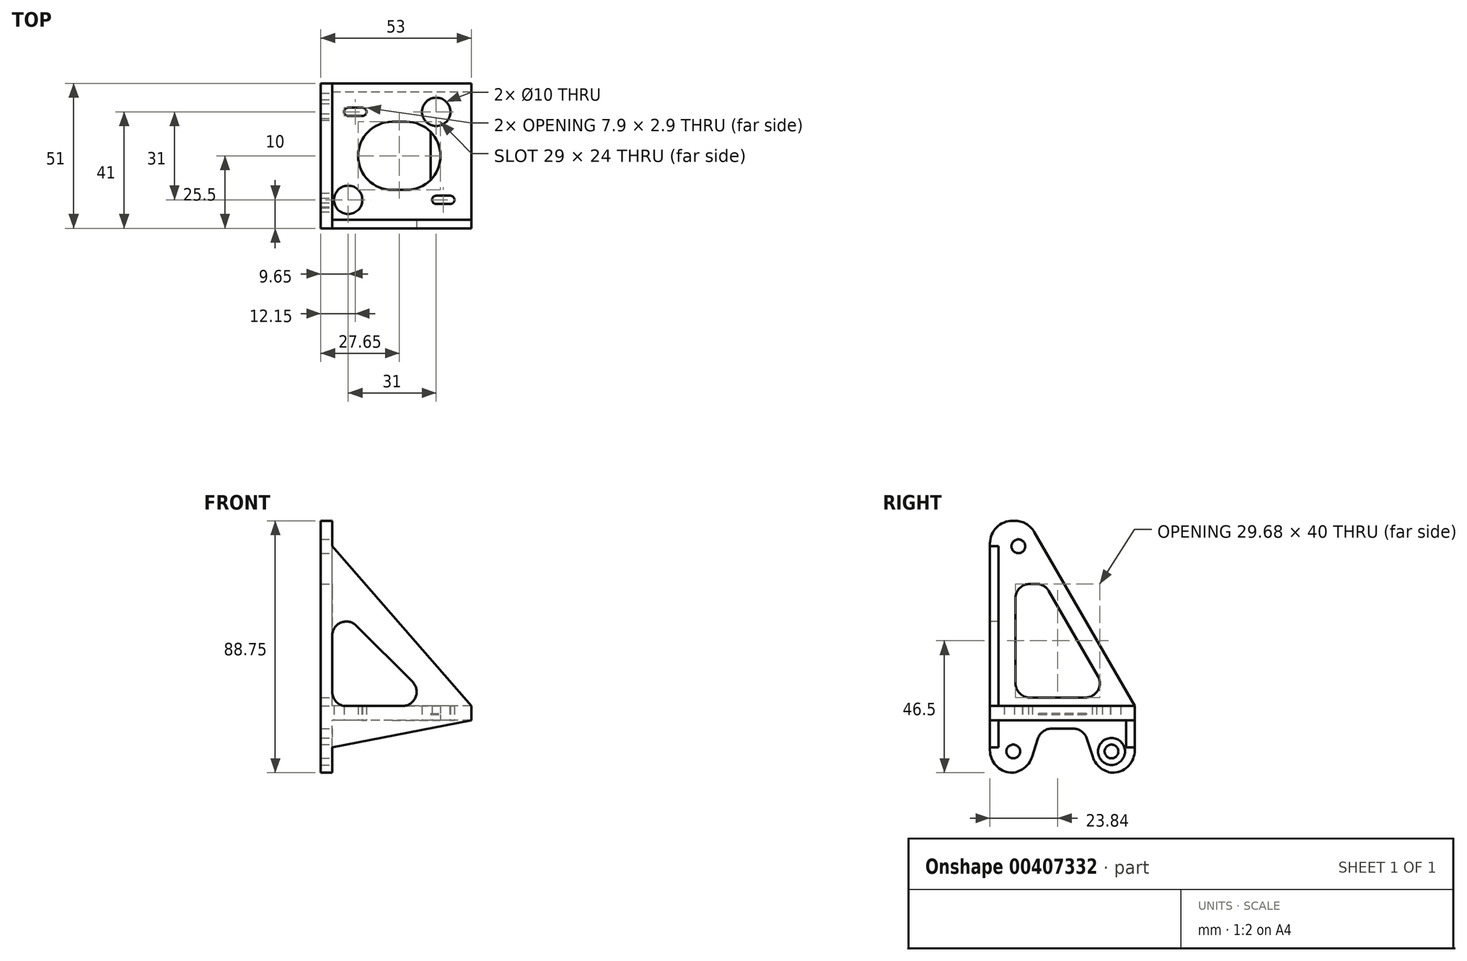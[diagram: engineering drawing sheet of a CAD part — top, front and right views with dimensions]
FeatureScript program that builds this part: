
annotation { "Feature Type Name" : "Feature", "Feature Type Description" : "" }
export const myFeature = defineFeature(function(context is Context, id is Id, definition is map)
    precondition{}
    {
        {
            var Q0;
            Q0=qCreatedBy(makeId("Right.planeOp"),FACE);
            var sketch = newSketch(context, id + "F0", { "sketchPlane" : qUnion([Q0])});
            skLineSegment(sketch, "E0", {"start": v(80, -40) * mm, "end": v(-40, -40) * mm, "construction": true});
            skLineSegment(sketch, "E1", {"start": v(-40, -40) * mm, "end": v(-40, 0) * mm, "construction": true});
            skLineSegment(sketch, "E2", {"start": v(-40, 0) * mm, "end": v(80, 0) * mm, "construction": true});
            skLineSegment(sketch, "E3", {"start": v(80, 0) * mm, "end": v(80, -40) * mm, "construction": true});
            skLineSegment(sketch, "E4", {"start": v(-40, 0) * mm, "end": v(0, 0) * mm, "construction": true});
            skLineSegment(sketch, "E5", {"start": v(0, 0) * mm, "end": v(0, 120) * mm, "construction": true});
            skLineSegment(sketch, "E6", {"start": v(0, 120) * mm, "end": v(-40, 120) * mm, "construction": true});
            skLineSegment(sketch, "E7", {"start": v(-40, 120) * mm, "end": v(-40, 0) * mm, "construction": true});
            skLineSegment(sketch, "E8", {"start": v(-20, -40) * mm, "end": v(-20, 0) * mm, "construction": true});
            skLineSegment(sketch, "E9", {"start": v(-20, -30) * mm, "end": v(-40, -30) * mm, "construction": true});
            skLineSegment(sketch, "E10", {"start": v(-14.5, -34.55) * mm, "end": v(-21.03, -34.55) * mm, "construction": true});
            skLineSegment(sketch, "E11", {"start": v(-21.03, -34.55) * mm, "end": v(-21.03, -33.52) * mm, "construction": true});
            skLineSegment(sketch, "E12", {"start": v(-14.5, -34.55) * mm, "end": v(-14.5, -20.46) * mm, "construction": true});
            skLineSegment(sketch, "E13", {"start": v(-21.03, -33.52) * mm, "end": v(-19.25, -33.52) * mm, "construction": true});
            skLineSegment(sketch, "E14", {"start": v(-19.25, -33.52) * mm, "end": v(-19.25, -26.47) * mm, "construction": true});
            skLineSegment(sketch, "E15", {"start": v(-19.25, -26.48) * mm, "end": v(-21.03, -26.48) * mm, "construction": true});
            skLineSegment(sketch, "E16", {"start": v(-21.03, -26.47) * mm, "end": v(-21.03, -20.46) * mm, "construction": true});
            skLineSegment(sketch, "E17", {"start": v(-21.03, -20.46) * mm, "end": v(-14.5, -20.46) * mm, "construction": true});
            skLineSegment(sketch, "E18", {"start": v(-20, -33.1) * mm, "end": v(-18.6, -33.1) * mm, "construction": true});
            skLineSegment(sketch, "E19", {"start": v(-18.6, -33.1) * mm, "end": v(-18.6, -26.9) * mm, "construction": true});
            skLineSegment(sketch, "E20", {"start": v(-18.6, -26.9) * mm, "end": v(-20, -26.9) * mm, "construction": true});
            skLineSegment(sketch, "E21", {"start": v(-20, -26.9) * mm, "end": v(-20, -33.1) * mm, "construction": true});
            skLineSegment(sketch, "E22", {"start": v(-14.5, -30) * mm, "end": v(-20, -30) * mm, "construction": true});
            skPoint(sketch, "E22.endSnap0", {"position": v(-20, -30) * mm});
            skLineSegment(sketch, "E23.MirrorCS", {"start": v(-14.5, -34.55) * mm, "end": v(-7.98, -34.55) * mm, "construction": true});
            skLineSegment(sketch, "E24.MirrorCS", {"start": v(-7.98, -34.55) * mm, "end": v(-7.98, -33.52) * mm, "construction": true});
            skLineSegment(sketch, "E25.MirrorCS", {"start": v(-7.98, -33.52) * mm, "end": v(-9.75, -33.52) * mm, "construction": true});
            skLineSegment(sketch, "E26.MirrorCS", {"start": v(-9.75, -33.52) * mm, "end": v(-9.75, -26.47) * mm, "construction": true});
            skLineSegment(sketch, "E27.MirrorCS", {"start": v(-10.4, -33.1) * mm, "end": v(-10.4, -26.9) * mm, "construction": true});
            skLineSegment(sketch, "E28.MirrorCS", {"start": v(-9, -26.9) * mm, "end": v(-9, -33.1) * mm, "construction": true});
            skLineSegment(sketch, "E29.MirrorCS", {"start": v(-9, -33.1) * mm, "end": v(-10.4, -33.1) * mm, "construction": true});
            skLineSegment(sketch, "E30.MirrorCS", {"start": v(-10.4, -26.9) * mm, "end": v(-9, -26.9) * mm, "construction": true});
            skLineSegment(sketch, "E31.MirrorCS", {"start": v(-9.75, -26.48) * mm, "end": v(-7.98, -26.48) * mm, "construction": true});
            skLineSegment(sketch, "E32.MirrorCS", {"start": v(-7.98, -26.47) * mm, "end": v(-7.98, -20.46) * mm, "construction": true});
            skLineSegment(sketch, "E33.MirrorCS", {"start": v(-7.98, -20.46) * mm, "end": v(-14.5, -20.46) * mm, "construction": true});
            skLineSegment(sketch, "E34", {"start": v(-37.22, -33.1) * mm, "end": v(14.04, -33.1) * mm, "construction": true});
            skLineSegment(sketch, "E35.MirrorCS", {"start": v(-37.22, -26.9) * mm, "end": v(14.04, -26.9) * mm, "construction": true});
            skLineSegment(sketch, "E36", {"start": v(-10, 0) * mm, "end": v(-10, 120) * mm, "construction": true});
            skLineSegment(sketch, "E37", {"start": v(-6.9, 0) * mm, "end": v(-6.9, 120) * mm, "construction": true});
            skLineSegment(sketch, "E38", {"start": v(-13.1, 120) * mm, "end": v(-13.1, 0) * mm, "construction": true});
            skLineSegment(sketch, "E39.MirrorCS", {"start": v(-26.9, 120) * mm, "end": v(-26.9, 0) * mm, "construction": true});
            skLineSegment(sketch, "E40.MirrorCS", {"start": v(-33.1, 0) * mm, "end": v(-33.1, 120) * mm, "construction": true});
            skLineSegment(sketch, "E41", {"start": v(6.62, -14) * mm, "end": v(-35.63, -14) * mm, "construction": true});
            skLineSegment(sketch, "E42", {"start": v(-35.63, -14) * mm, "end": v(-35.63, 33.25) * mm, "construction": true});
            skLineSegment(sketch, "E43", {"start": v(-35.63, 33.25) * mm, "end": v(6.62, 33.25) * mm, "construction": true});
            skLineSegment(sketch, "E44", {"start": v(6.62, 33.25) * mm, "end": v(6.63, -14) * mm, "construction": true});
            skLineSegment(sketch, "E45", {"start": v(-14.5, -14) * mm, "end": v(-14.5, 33.25) * mm, "construction": true});
            skLineSegment(sketch, "E46", {"start": v(-1, -14) * mm, "end": v(-1, -10) * mm, "construction": true});
            skLineSegment(sketch, "E47", {"start": v(3, -10) * mm, "end": v(-1, -10) * mm, "construction": true});
            skLineSegment(sketch, "E48", {"start": v(3, -10) * mm, "end": v(3, -14) * mm, "construction": true});
            skLineSegment(sketch, "E49", {"start": v(1, -10) * mm, "end": v(1, -14) * mm, "construction": true});
            skLineSegment(sketch, "E50.MirrorCS", {"start": v(-32, -10) * mm, "end": v(-32, -14) * mm, "construction": true});
            skLineSegment(sketch, "E51.MirrorCS", {"start": v(-32, -10) * mm, "end": v(-28, -10) * mm, "construction": true});
            skLineSegment(sketch, "E52.MirrorCS", {"start": v(-30, -10) * mm, "end": v(-30, -14) * mm, "construction": true});
            skLineSegment(sketch, "E53.MirrorCS", {"start": v(-28, -14) * mm, "end": v(-28, -10) * mm, "construction": true});
            skLineSegment(sketch, "E54", {"start": v(-3.5, -14) * mm, "end": v(-3.5, -16) * mm, "construction": true});
            skLineSegment(sketch, "E55", {"start": v(-3.5, -16) * mm, "end": v(-25.5, -16) * mm, "construction": true});
            skLineSegment(sketch, "E56", {"start": v(-25.5, -16) * mm, "end": v(-25.5, -14) * mm, "construction": true});
            skLineSegment(sketch, "E57", {"start": v(-12.25, -16) * mm, "end": v(-12.25, -38) * mm, "construction": true});
            skLineSegment(sketch, "E58", {"start": v(-12.25, -38) * mm, "end": v(-16.75, -38) * mm, "construction": true});
            skLineSegment(sketch, "E59", {"start": v(-16.75, -38) * mm, "end": v(-16.75, -16) * mm, "construction": true});
            skLineSegment(sketch, "E60", {"start": v(-31.3, 51.25) * mm, "end": v(-40, 51.25) * mm});
            skLineSegment(sketch, "E61", {"start": v(-40, 51.25) * mm, "end": v(-40, -37.5) * mm});
            skLineSegment(sketch, "E62", {"start": v(-40, -37.5) * mm, "end": v(-32.83, -37.5) * mm});
            skLineSegment(sketch, "E63", {"start": v(-25.21, -31.96) * mm, "end": v(-23.12, -25.46) * mm});
            skLineSegment(sketch, "E64", {"start": v(3.83, -37.5) * mm, "end": v(11, -37.5) * mm});
            skLineSegment(sketch, "E65", {"start": v(11, -37.5) * mm, "end": v(11, -14) * mm});
            skCircle(sketch, "E66", {"center": v(-31.8, -30) * mm, "radius": 2.43 * mm});
            skCircle(sketch, "E67.MirrorC", {"center": v(2.8, -30) * mm, "radius": 2.43 * mm});
            skLineSegment(sketch, "E68", {"start": v(-37, -37.5) * mm, "end": v(-37, 51.25) * mm});
            skLineSegment(sketch, "E69", {"start": v(-37, -14) * mm, "end": v(11, -14) * mm});
            skLineSegment(sketch, "E70.MirrorCS", {"start": v(-3.79, -31.96) * mm, "end": v(-5.88, -25.46) * mm});
            skLineSegment(sketch, "E71", {"start": v(-10.64, -22) * mm, "end": v(-18.36, -22) * mm});
            skCircle(sketch, "E72", {"center": v(-31.8, -30) * mm, "radius": 4.75 * mm});
            skCircle(sketch, "E73.MirrorC", {"center": v(2.8, -30) * mm, "radius": 4.75 * mm});
            skLineSegment(sketch, "E74", {"start": v(-37, -19) * mm, "end": v(11, -19) * mm});
            skLineSegment(sketch, "E75.MirrorCS", {"start": v(8, -37.5) * mm, "end": v(8, -14) * mm});
            skCircle(sketch, "E76", {"center": v(-30, 42.25) * mm, "radius": 2.43 * mm});
            skCircle(sketch, "E77", {"center": v(-30, 42.25) * mm, "radius": 4.75 * mm, "construction": true});
            skLineSegment(sketch, "E78", {"start": v(-30, 0) * mm, "end": v(-30, 120) * mm, "construction": true});
            skLineSegment(sketch, "E79", {"start": v(11, -14) * mm, "end": v(-24.36, 47.25) * mm});
            skLineSegment(sketch, "E80", {"start": v(-6.32, -11) * mm, "end": v(-26, -11) * mm});
            skLineSegment(sketch, "E81", {"start": v(-31, -6) * mm, "end": v(-31, 24) * mm});
            skLineSegment(sketch, "E82", {"start": v(-19.31, 26.5) * mm, "end": v(-2, -3.5) * mm});
            skArc(sketch, "E83.filletArc", {"start": v(-6.32, -11) * mm, "mid": v(-2, -8.5) * mm, "end": v(-2, -3.5) * mm});
            skArc(sketch, "E84.filletArc", {"start": v(-31, -6) * mm, "mid": v(-29.54, -9.54) * mm, "end": v(-26, -11) * mm});
            skLineSegment(sketch, "E85", {"start": v(-23.64, 29) * mm, "end": v(-26, 29) * mm});
            skArc(sketch, "E86.filletArc", {"start": v(-26, 29) * mm, "mid": v(-29.54, 27.54) * mm, "end": v(-31, 24) * mm});
            skPoint(sketch, "E87.visualSharp", {"position": v(-20.75, 29) * mm});
            skArc(sketch, "E87.filletArc", {"start": v(-19.31, 26.5) * mm, "mid": v(-21.14, 28.33) * mm, "end": v(-23.64, 29) * mm});
            skPoint(sketch, "E88.visualSharp", {"position": v(-7, -22) * mm});
            skArc(sketch, "E88.filletArc", {"start": v(-5.88, -25.46) * mm, "mid": v(-7.7, -22.96) * mm, "end": v(-10.64, -22) * mm});
            skPoint(sketch, "E89.visualSharp", {"position": v(-22, -22) * mm});
            skArc(sketch, "E89.filletArc", {"start": v(-18.36, -22) * mm, "mid": v(-21.3, -22.96) * mm, "end": v(-23.12, -25.46) * mm});
            skPoint(sketch, "E90.visualSharp", {"position": v(-2, -37.5) * mm});
            skArc(sketch, "E90.filletArc", {"start": v(-3.79, -31.96) * mm, "mid": v(-0.88, -35.97) * mm, "end": v(3.83, -37.5) * mm});
            skPoint(sketch, "E91.visualSharp", {"position": v(-27, -37.5) * mm});
            skArc(sketch, "E91.filletArc", {"start": v(-32.83, -37.5) * mm, "mid": v(-28.12, -35.97) * mm, "end": v(-25.21, -31.96) * mm});
            skPoint(sketch, "E92.visualSharp", {"position": v(-26.67, 51.25) * mm});
            skArc(sketch, "E92.filletArc", {"start": v(-24.36, 47.25) * mm, "mid": v(-27.3, 50.18) * mm, "end": v(-31.3, 51.25) * mm});
            skSolve(sketch);
        }
        {
            var Q0;
            Q0=makeQuery(id+"F0.imprint","IMPRINT",FACE,{"disambiguationData":[TD([[makeQuery(id+"F0.imprint","IMPRINT",EDGE,{"derivedFrom":sQuery(id+"F0.wireOp",EDGE,"E76")}),-1.0]])]});
            var Q1;
            {var subQ6=sQuery(id+"F0.wireOp",EDGE,"E63");Q1=makeQuery(id+"F0.imprint","IMPRINT",FACE,{"disambiguationData":[TD([[makeQuery(id+"F0.imprint","IMPRINT",EDGE,{"derivedFrom":subQ6}),1.0]])]});}
            var Q2;
            {var subQ0=sQuery(id+"F0.wireOp",EDGE,"E65");var subQ1=sQuery(id+"F0.wireOp",EDGE,"E64");var subQ2=makeQuery(id+"F0.imprint","INTERSECT",VERTEX,{"derivedFrom":[subQ1,subQ0]});Q2=makeQuery(id+"F0.imprint","IMPRINT",FACE,{"disambiguationData":[TD([[makeQuery(id+"F0.imprint","IMPRINT",EDGE,{"disambiguationData":[TD([[subQ2,1.0]])],"derivedFrom":subQ1}),1.0]])]});}
            var Q3;
            {var subQ1=sQuery(id+"F0.wireOp",EDGE,"E65");var subQ3=sQuery(id+"F0.wireOp",EDGE,"E74");var subQ4=makeQuery(id+"F0.imprint","INTERSECT",VERTEX,{"derivedFrom":[subQ1,subQ3]});Q3=makeQuery(id+"F0.imprint","IMPRINT",FACE,{"disambiguationData":[TD([[makeQuery(id+"F0.imprint","IMPRINT",EDGE,{"disambiguationData":[TD([[subQ4,1.0]])],"derivedFrom":subQ3}),1.0]])]});}
            var Q4;
            {var subQ0=sQuery(id+"F0.wireOp",EDGE,"E69");var subQ1=sQuery(id+"F0.wireOp",EDGE,"E68");var subQ2=makeQuery(id+"F0.imprint","INTERSECT",VERTEX,{"derivedFrom":[subQ1,subQ0]});Q4=makeQuery(id+"F0.imprint","IMPRINT",FACE,{"disambiguationData":[TD([[makeQuery(id+"F0.imprint","IMPRINT",EDGE,{"disambiguationData":[TD([[subQ2,1.0]])],"derivedFrom":subQ1}),-1.0]])]});}
            var Q5;
            {var subQ1=sQuery(id+"F0.wireOp",EDGE,"E61");Q5=makeQuery(id+"F0.imprint","IMPRINT",FACE,{"disambiguationData":[TD([[makeQuery(id+"F0.imprint","IMPRINT",EDGE,{"derivedFrom":subQ1}),1.0]])]});}
            var Q6;
            Q6=makeQuery(id+"F0.imprint","IMPRINT",FACE,{"disambiguationData":[TD([[makeQuery(id+"F0.imprint","IMPRINT",EDGE,{"derivedFrom":sQuery(id+"F0.wireOp",EDGE,"E67.MirrorC")}),1.0]])]});
            var Q7;
            Q7=makeQuery(id+"F0.imprint","IMPRINT",FACE,{"disambiguationData":[TD([[makeQuery(id+"F0.imprint","IMPRINT",EDGE,{"derivedFrom":sQuery(id+"F0.wireOp",EDGE,"E66")}),-1.0]])]});
            extrude(context, id + "F1", {"entities" : qUnion([Q0, Q1, Q2, Q3, Q4, Q5, Q6, Q7]), "oppositeDirection" : true, "depth" : 4 * mm});
        }
        {
            var Q0;
            {var subQ1=sQuery(id+"F0.wireOp",EDGE,"E61");Q0=makeQuery(id+"F0.imprint","IMPRINT",FACE,{"disambiguationData":[TD([[makeQuery(id+"F0.imprint","IMPRINT",EDGE,{"derivedFrom":subQ1}),1.0]])]});}
            var Q1;
            {var subQ0=sQuery(id+"F0.wireOp",EDGE,"E65");var subQ1=sQuery(id+"F0.wireOp",EDGE,"E64");var subQ2=makeQuery(id+"F0.imprint","INTERSECT",VERTEX,{"derivedFrom":[subQ1,subQ0]});Q1=makeQuery(id+"F0.imprint","IMPRINT",FACE,{"disambiguationData":[TD([[makeQuery(id+"F0.imprint","IMPRINT",EDGE,{"disambiguationData":[TD([[subQ2,1.0]])],"derivedFrom":subQ1}),1.0]])]});}
            var Q2;
            {var subQ1=sQuery(id+"F0.wireOp",EDGE,"E65");var subQ3=sQuery(id+"F0.wireOp",EDGE,"E74");var subQ4=makeQuery(id+"F0.imprint","INTERSECT",VERTEX,{"derivedFrom":[subQ1,subQ3]});Q2=makeQuery(id+"F0.imprint","IMPRINT",FACE,{"disambiguationData":[TD([[makeQuery(id+"F0.imprint","IMPRINT",EDGE,{"disambiguationData":[TD([[subQ4,1.0]])],"derivedFrom":subQ3}),1.0]])]});}
            var Q3;
            {var subQ0=sQuery(id+"F0.wireOp",EDGE,"E69");var subQ1=sQuery(id+"F0.wireOp",EDGE,"E68");var subQ2=makeQuery(id+"F0.imprint","INTERSECT",VERTEX,{"derivedFrom":[subQ1,subQ0]});Q3=makeQuery(id+"F0.imprint","IMPRINT",FACE,{"disambiguationData":[TD([[makeQuery(id+"F0.imprint","IMPRINT",EDGE,{"disambiguationData":[TD([[subQ2,1.0]])],"derivedFrom":subQ1}),-1.0]])]});}
            extrude(context, id + "F2", {"entities" : qUnion([Q0, Q1, Q2, Q3]), "operationType" : NewBodyOperationType.ADD, "offsetDistance" : 25 * mm, "depth" : 49 * mm});
        }
        {
            var Q0;
            {var subQ0=sQuery(id+"F0.wireOp",EDGE,"E61");Q0=makeQuery(id+"F2.boolean.opBoolean","MERGE",FACE,{"derivedFrom":[makeQuery(id+"F1.opExtrude","SWEPT_FACE",FACE,{"disambiguationData":[OSD([subQ0])]}),makeQuery(id+"F2.opExtrude","SWEPT_FACE",FACE,{"disambiguationData":[OSD([subQ0])]})]});}
            var sketch = newSketch(context, id + "F3", { "sketchPlane" : qUnion([Q0])});
            skLineSegment(sketch, "E93", {"start": v(49, -19) * mm, "end": v(0, -28.5) * mm});
            skLineSegment(sketch, "E94", {"start": v(49, -14) * mm, "end": v(0, 42.25) * mm});
            skLineSegment(sketch, "E95.0.0", {"start": v(0, -9) * mm, "end": v(0, 10.75) * mm});
            skLineSegment(sketch, "E95.0.2", {"start": v(49, 51.25) * mm, "end": v(49, -14) * mm});
            skLineSegment(sketch, "E95.0.3", {"start": v(24.75, -14) * mm, "end": v(5, -14) * mm});
            skLineSegment(sketch, "E96.0.0", {"start": v(0, -28.5) * mm, "end": v(0, -19) * mm});
            skLineSegment(sketch, "E96.0.1", {"start": v(0, -19) * mm, "end": v(49, -19) * mm});
            skLineSegment(sketch, "E96.0.2", {"start": v(49, -19) * mm, "end": v(49, -37.5) * mm});
            skLineSegment(sketch, "E97", {"start": v(28.29, -5.46) * mm, "end": v(8.54, 14.29) * mm});
            skArc(sketch, "E98.filletArc", {"start": v(8.54, 14.29) * mm, "mid": v(3.09, 15.37) * mm, "end": v(0, 10.75) * mm});
            skArc(sketch, "E99.filletArc", {"start": v(24.75, -14) * mm, "mid": v(29.37, -10.91) * mm, "end": v(28.29, -5.46) * mm});
            skPoint(sketch, "E100.visualSharp", {"position": v(0, -14) * mm});
            skArc(sketch, "E100.filletArc", {"start": v(0, -9) * mm, "mid": v(1.46, -12.54) * mm, "end": v(5, -14) * mm});
            skLineSegment(sketch, "E101", {"start": v(0, 42.25) * mm, "end": v(0, 51.25) * mm});
            skLineSegment(sketch, "E102", {"start": v(0, 51.25) * mm, "end": v(49, 51.25) * mm});
            skLineSegment(sketch, "E103", {"start": v(0, -28.5) * mm, "end": v(0, -37.5) * mm});
            skLineSegment(sketch, "E104", {"start": v(0, -37.5) * mm, "end": v(49, -37.5) * mm});
            skSolve(sketch);
        }
        {
            var Q0;
            Q0=makeQuery(id+"F3.imprint","IMPRINT",FACE,{"disambiguationData":[TD([[makeQuery(id+"F3.imprint","IMPRINT",EDGE,{"derivedFrom":sQuery(id+"F3.wireOp",EDGE,"E93")}),1.0]])]});
            var Q1;
            Q1=makeQuery(id+"F3.imprint","IMPRINT",FACE,{"disambiguationData":[TD([[makeQuery(id+"F3.imprint","IMPRINT",EDGE,{"derivedFrom":sQuery(id+"F3.wireOp",EDGE,"E94")}),-1.0]])]});
            var Q2;
            Q2=makeQuery(id+"F3.imprint","IMPRINT",FACE,{"disambiguationData":[TD([[makeQuery(id+"F3.imprint","IMPRINT",EDGE,{"derivedFrom":sQuery(id+"F3.wireOp",EDGE,"E95.0.0")}),-1.0]])]});
            extrude(context, id + "F4", {"entities" : qUnion([Q0, Q1, Q2]), "operationType" : NewBodyOperationType.REMOVE, "endBound" : BoundingType.THROUGH_ALL, "oppositeDirection" : true, "depth" : 25 * mm});
        }
        {
            var Q0;
            Q0=makeQuery(id+"F0.imprint","IMPRINT",FACE,{"disambiguationData":[TD([[makeQuery(id+"F0.imprint","IMPRINT",EDGE,{"derivedFrom":sQuery(id+"F0.wireOp",EDGE,"E67.MirrorC")}),1.0]])]});
            var Q1;
            Q1=makeQuery(id+"F0.imprint","IMPRINT",FACE,{"disambiguationData":[TD([[makeQuery(id+"F0.imprint","IMPRINT",EDGE,{"derivedFrom":sQuery(id+"F0.wireOp",EDGE,"E66")}),1.0]])]});
            var Q2;
            Q2=makeQuery(id+"F0.imprint","IMPRINT",FACE,{"disambiguationData":[TD([[makeQuery(id+"F0.imprint","IMPRINT",EDGE,{"derivedFrom":sQuery(id+"F0.wireOp",EDGE,"E66")}),-1.0]])]});
            var Q3;
            Q3=makeQuery(id+"F0.imprint","IMPRINT",FACE,{"disambiguationData":[TD([[makeQuery(id+"F0.imprint","IMPRINT",EDGE,{"derivedFrom":sQuery(id+"F0.wireOp",EDGE,"E67.MirrorC")}),-1.0]])]});
            extrude(context, id + "F5", {"entities" : qUnion([Q0, Q1, Q2, Q3]), "operationType" : NewBodyOperationType.REMOVE, "endBound" : BoundingType.THROUGH_ALL, "depth" : 25 * mm});
        }
        {
            var Q0;
            Q0=makeQuery(id+"F2.opExtrude","SWEPT_FACE",FACE,{"disambiguationData":[OSD([sQuery(id+"F0.wireOp",EDGE,"E74")])]});
            var sketch = newSketch(context, id + "F6", { "sketchPlane" : qUnion([Q0])});
            skLineSegment(sketch, "E105.0", {"start": v(49, 37) * mm, "end": v(49, -8) * mm, "construction": true});
            skLineSegment(sketch, "E106", {"start": v(0, 14.5) * mm, "end": v(49, 14.5) * mm, "construction": true});
            skLineSegment(sketch, "E107", {"start": v(21.15, 37) * mm, "end": v(21.15, -8) * mm, "construction": true});
            skArc(sketch, "E108", {"start": v(5.65, 0.45) * mm, "mid": v(4.2, -1) * mm, "end": v(5.65, -2.45) * mm});
            skArc(sketch, "E109.MirrorC", {"start": v(36.65, -2.45) * mm, "mid": v(35.2, -1) * mm, "end": v(36.65, 0.45) * mm});
            skArc(sketch, "E110.MirrorC", {"start": v(36.65, 31.45) * mm, "mid": v(35.2, 30) * mm, "end": v(36.65, 28.55) * mm});
            skCircle(sketch, "E111", {"center": v(5.65, -1) * mm, "radius": 5 * mm});
            skCircle(sketch, "E112.MirrorC", {"center": v(5.65, 30) * mm, "radius": 5 * mm});
            skCircle(sketch, "E113.MirrorC", {"center": v(36.65, -1) * mm, "radius": 5 * mm});
            skCircle(sketch, "E114.MirrorC", {"center": v(36.65, 30) * mm, "radius": 5 * mm});
            skCircle(sketch, "E115", {"center": v(21.15, 14.5) * mm, "radius": 12 * mm});
            skLineSegment(sketch, "E116.0", {"start": v(0, 37) * mm, "end": v(0, -8) * mm, "construction": true});
            skLineSegment(sketch, "E117", {"start": v(26.15, 37) * mm, "end": v(26.15, -8) * mm, "construction": true});
            skArc(sketch, "E118.converted", {"start": v(5.65, 28.55) * mm, "mid": v(4.2, 30) * mm, "end": v(5.65, 31.45) * mm});
            skArc(sketch, "E119.1.0.0", {"start": v(10.44, 31.43) * mm, "mid": v(12.1, 30) * mm, "end": v(10.44, 28.57) * mm});
            skLineSegment(sketch, "E119.direction1", {"start": v(5.65, 30) * mm, "end": v(10.65, 30) * mm, "construction": true});
            skLineSegment(sketch, "E120", {"start": v(5.65, 31.45) * mm, "end": v(10.65, 31.45) * mm});
            skLineSegment(sketch, "E121", {"start": v(5.65, 28.55) * mm, "end": v(10.65, 28.55) * mm});
            skArc(sketch, "E122", {"start": v(26.15, 2.5) * mm, "mid": v(38.15, 14.5) * mm, "end": v(26.15, 26.5) * mm});
            skLineSegment(sketch, "E123", {"start": v(21.15, 26.5) * mm, "end": v(26.15, 26.5) * mm});
            skLineSegment(sketch, "E124", {"start": v(26.15, 2.5) * mm, "end": v(21.15, 2.5) * mm});
            skArc(sketch, "E125.1.0.0", {"start": v(41.44, 28.57) * mm, "mid": v(43.1, 30) * mm, "end": v(41.44, 31.43) * mm});
            skLineSegment(sketch, "E125.direction1", {"start": v(36.65, 30) * mm, "end": v(41.65, 30) * mm, "construction": true});
            skLineSegment(sketch, "E126", {"start": v(36.65, 31.45) * mm, "end": v(41.65, 31.45) * mm});
            skLineSegment(sketch, "E127", {"start": v(41.65, 28.55) * mm, "end": v(36.65, 28.55) * mm});
            skLineSegment(sketch, "E128.MirrorCS", {"start": v(41.65, 0.45) * mm, "end": v(36.65, 0.45) * mm});
            skArc(sketch, "E129.MirrorCS", {"start": v(41.44, 0.43) * mm, "mid": v(43.1, -1) * mm, "end": v(41.44, -2.43) * mm});
            skLineSegment(sketch, "E130.MirrorCS", {"start": v(36.65, -2.45) * mm, "end": v(41.65, -2.45) * mm});
            skLineSegment(sketch, "E131.MirrorCS", {"start": v(5.65, -2.45) * mm, "end": v(10.65, -2.45) * mm});
            skArc(sketch, "E132.MirrorCS", {"start": v(10.44, -2.43) * mm, "mid": v(12.1, -1) * mm, "end": v(10.44, 0.43) * mm});
            skLineSegment(sketch, "E133.MirrorCS", {"start": v(5.65, 0.45) * mm, "end": v(10.65, 0.45) * mm});
            skPoint(sketch, "E134.orphan", {"position": v(38.15, 19.5) * mm});
            skPoint(sketch, "E135.orphan", {"position": v(38.15, 9.5) * mm});
            skPoint(sketch, "E136.visualSharp", {"position": v(38.15, 26.5) * mm});
            skPoint(sketch, "E137.visualSharp", {"position": v(38.15, 2.5) * mm});
            skLineSegment(sketch, "E138", {"start": v(34.65, 22.97) * mm, "end": v(34.65, 6.03) * mm});
            skSolve(sketch);
        }
        {
            var Q0;
            Q0=makeQuery(id+"F6.imprint","IMPRINT",FACE,{"disambiguationData":[TD([[makeQuery(id+"F6.imprint","IMPRINT",EDGE,{"derivedFrom":sQuery(id+"F6.wireOp",EDGE,"c21952d8-def6-47bd-b765-fc192d1d6f750.MirrorC")}),-1.0]])]});
            var Q1;
            Q1=makeQuery(id+"F6.imprint","IMPRINT",FACE,{"disambiguationData":[TD([[makeQuery(id+"F6.imprint","IMPRINT",EDGE,{"derivedFrom":sQuery(id+"F6.wireOp",EDGE,"E108")}),1.0]])]});
            var Q2;
            Q2=makeQuery(id+"F6.imprint","IMPRINT",FACE,{"disambiguationData":[TD([[makeQuery(id+"F6.imprint","IMPRINT",EDGE,{"derivedFrom":sQuery(id+"F6.wireOp",EDGE,"E109.MirrorC")}),-1.0]])]});
            var Q3;
            Q3=makeQuery(id+"F6.imprint","IMPRINT",FACE,{"disambiguationData":[TD([[makeQuery(id+"F6.imprint","IMPRINT",EDGE,{"derivedFrom":sQuery(id+"F6.wireOp",EDGE,"E110.MirrorC")}),1.0]])]});
            var Q4;
            Q4=makeQuery(id+"F6.imprint","IMPRINT",FACE,{"disambiguationData":[TD([[makeQuery(id+"F6.imprint","IMPRINT",EDGE,{"derivedFrom":sQuery(id+"F6.wireOp",EDGE,"E115")}),1.0]])]});
            var Q5;
            {var subQ0=sQuery(id+"F6.wireOp",EDGE,"E118.converted");Q5=makeQuery(id+"F6.imprint","IMPRINT",FACE,{"disambiguationData":[TD([[makeQuery(id+"F6.imprint","IMPRINT",EDGE,{"derivedFrom":subQ0}),-1.0]])]});}
            var Q6;
            {var subQ0=sQuery(id+"F6.wireOp",EDGE,"E119.1.0.0");var subQ1=sQuery(id+"F6.wireOp",EDGE,"E112.MirrorC");var subQ2=makeQuery(id+"F6.imprint","INTERSECT",VERTEX,{"disambiguationData":[OD(0.0)],"derivedFrom":[subQ1,subQ0]});Q6=makeQuery(id+"F6.imprint","IMPRINT",FACE,{"disambiguationData":[TD([[makeQuery(id+"F6.imprint","IMPRINT",EDGE,{"disambiguationData":[TD([[subQ2,-1.0]])],"derivedFrom":subQ1}),1.0]])]});}
            var Q7;
            {var subQ0=sQuery(id+"F6.wireOp",EDGE,"E125.1.0.0");var subQ1=sQuery(id+"F6.wireOp",EDGE,"E114.MirrorC");var subQ2=makeQuery(id+"F6.imprint","INTERSECT",VERTEX,{"disambiguationData":[OD(0.0)],"derivedFrom":[subQ1,subQ0]});Q7=makeQuery(id+"F6.imprint","IMPRINT",FACE,{"disambiguationData":[TD([[makeQuery(id+"F6.imprint","IMPRINT",EDGE,{"disambiguationData":[TD([[subQ2,-1.0]])],"derivedFrom":subQ1}),-1.0]])]});}
            var Q8;
            {var subQ0=sQuery(id+"F6.wireOp",EDGE,"E129.MirrorCS");var subQ1=sQuery(id+"F6.wireOp",EDGE,"E113.MirrorC");var subQ2=makeQuery(id+"F6.imprint","INTERSECT",VERTEX,{"disambiguationData":[OD(0.0)],"derivedFrom":[subQ1,subQ0]});Q8=makeQuery(id+"F6.imprint","IMPRINT",FACE,{"disambiguationData":[TD([[makeQuery(id+"F6.imprint","IMPRINT",EDGE,{"disambiguationData":[TD([[subQ2,-1.0]])],"derivedFrom":subQ1}),1.0]])]});}
            var Q9;
            {var subQ0=sQuery(id+"F6.wireOp",EDGE,"E132.MirrorCS");var subQ1=sQuery(id+"F6.wireOp",EDGE,"E111");var subQ2=makeQuery(id+"F6.imprint","INTERSECT",VERTEX,{"disambiguationData":[OD(0.0)],"derivedFrom":[subQ1,subQ0]});Q9=makeQuery(id+"F6.imprint","IMPRINT",FACE,{"disambiguationData":[TD([[makeQuery(id+"F6.imprint","IMPRINT",EDGE,{"disambiguationData":[TD([[subQ2,-1.0]])],"derivedFrom":subQ1}),-1.0]])]});}
            var Q10;
            Q10=makeQuery(id+"F6.imprint","IMPRINT",FACE,{"disambiguationData":[TD([[makeQuery(id+"F6.imprint","IMPRINT",EDGE,{"derivedFrom":sQuery(id+"F6.wireOp",EDGE,"E122")}),1.0]])]});
            var Q11;
            {var subQ5=sQuery(id+"F6.wireOp",EDGE,"E136.filletArc");Q11=makeQuery(id+"F6.imprint","IMPRINT",FACE,{"disambiguationData":[TD([[makeQuery(id+"F6.imprint","IMPRINT",EDGE,{"derivedFrom":subQ5}),1.0]])]});}
            var Q12;
            {var subQ5=sQuery(id+"F6.wireOp",EDGE,"E137.filletArc");Q12=makeQuery(id+"F6.imprint","IMPRINT",FACE,{"disambiguationData":[TD([[makeQuery(id+"F6.imprint","IMPRINT",EDGE,{"derivedFrom":subQ5}),1.0]])]});}
            var Q13;
            {var subQ0=sQuery(id+"F6.wireOp",EDGE,"E138");Q13=makeQuery(id+"F6.imprint","IMPRINT",FACE,{"disambiguationData":[TD([[makeQuery(id+"F6.imprint","IMPRINT",EDGE,{"derivedFrom":subQ0}),1.0]])]});}
            extrude(context, id + "F7", {"entities" : qUnion([Q0, Q1, Q2, Q3, Q4, Q5, Q6, Q7, Q8, Q9, Q10, Q11, Q12, Q13]), "operationType" : NewBodyOperationType.REMOVE, "endBound" : BoundingType.THROUGH_ALL, "oppositeDirection" : true, "offsetDistance" : 25 * mm, "depth" : 25 * mm, "hasSecondDirection" : true, "secondDirectionBound" : SecondDirectionBoundingType.THROUGH_ALL, "secondDirectionOppositeDirection" : false, "secondDirectionDepth" : 25 * mm});
        }
        {
            var Q0;
            {var subQ0=sQuery(id+"F0.wireOp",EDGE,"E61");var subQ1=sQuery(id+"F0.wireOp",EDGE,"E60");Q0=makeQuery(id+"F2.boolean.opBoolean","MERGE",EDGE,{"derivedFrom":[makeQuery(id+"F1.opExtrude","SWEPT_EDGE",EDGE,{"disambiguationData":[OSD([subQ1,subQ0])]}),makeQuery(id+"F2.opExtrude","SWEPT_EDGE",EDGE,{"disambiguationData":[OSD([subQ1,subQ0])]})]});}
            var Q1;
            {var subQ0=sQuery(id+"F0.wireOp",EDGE,"E62");var subQ1=sQuery(id+"F0.wireOp",EDGE,"E61");Q1=makeQuery(id+"F2.boolean.opBoolean","MERGE",EDGE,{"derivedFrom":[makeQuery(id+"F1.opExtrude","SWEPT_EDGE",EDGE,{"disambiguationData":[OSD([subQ1,subQ0])]}),makeQuery(id+"F2.opExtrude","SWEPT_EDGE",EDGE,{"disambiguationData":[OSD([subQ1,subQ0])]})]});}
            var Q2;
            {var subQ0=sQuery(id+"F0.wireOp",EDGE,"E65");var subQ1=sQuery(id+"F0.wireOp",EDGE,"E64");Q2=makeQuery(id+"F2.boolean.opBoolean","MERGE",EDGE,{"derivedFrom":[makeQuery(id+"F1.opExtrude","SWEPT_EDGE",EDGE,{"disambiguationData":[OSD([subQ1,subQ0])]}),makeQuery(id+"F2.opExtrude","SWEPT_EDGE",EDGE,{"disambiguationData":[OSD([subQ1,subQ0])]})]});}
            fillet(context, id + "F8", {"entities" : qUnion([Q0, Q1, Q2]), "radius" : 8 * mm, "tangentPropagation" : true, "allowEdgeOverflow" : false});
        }
        {
            var Q0;
            {var subQ0=sQuery(id+"F6.wireOp",EDGE,"E138");Q0=makeQuery(id+"F6.imprint","IMPRINT",FACE,{"disambiguationData":[TD([[makeQuery(id+"F6.imprint","IMPRINT",EDGE,{"derivedFrom":subQ0}),1.0]])]});}
            extrude(context, id + "F9", {"entities" : qUnion([Q0]), "operationType" : NewBodyOperationType.ADD, "oppositeDirection" : true, "depth" : 2.4 * mm, "offsetDistance" : 25 * mm, "hasSecondDirection" : true, "secondDirectionOppositeDirection" : true, "secondDirectionDepth" : 2 * mm});
        }
    });
